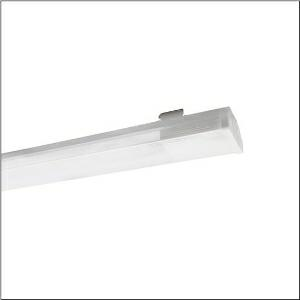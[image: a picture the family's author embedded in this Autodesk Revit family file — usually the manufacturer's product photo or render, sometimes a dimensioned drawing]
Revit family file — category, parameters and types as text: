
# Revit family: modario_r__31_gen_2_53bm811du4gxc2_c2e7
name_source: partatom
category: Lighting Fixtures
units: mm (PartAtom-declared; Revit-internal decimal feet)

## family parameters
Cut with Voids When Loaded = No
Host = Face
Light Source = No
Part Type = Normal
Room Calculation Point = No
Round Connector Dimension = Use Diameter
Shared = No

## types (1)
- --- (1 x LED, 16290 lm, 92.1 W, 4000K)
    Apparent Load = 92 VA
    CIE Flux Codes = 50 78 94 90 100
    Color Rendering = 80
    Color Temperature = 4000K
    Default Elevation = 1800 mm
    Description = Modario® 31 Gen.2, luminaire insert, of sheet steel, coil coated, white, length: 2.392mm, width: 81mm, height: 82mm, 8x system unit, system units: 299mm, LED rated luminous flux: 16.290lm, light colour: 840, control gear: DALI 2, control gear: ECG DALI, with plug, 5-pole, with phase selection, mains connection: 220..240V, AC, 50/60Hz, rated input power: 92W, through-wiring accessed according to module size, primary optical cover: cover, of PMMA, light emission: direct distribution, primary light characteristic: symmetric, protection rating (complete): IP20, protection rating (LED compartment): IP50, insulation class (complete): insulation class I (protective earthing), certification: CE, ENEC, VDE, UKCA, impact resistance: IK03, permissible ambient temperature for indoor applications: -25..+40°C, corresponds to IFS (International Featured Standards) requirements for safety and quality in the food industry, reducing of maximum allowable ambient temperature of 5°C with ceiling mounting, packaging unit: 1 piece
    Height = 92 mm
    Lamp = 1 x LED
    Lamp Light Flux = 16290 lm
    Lamp Power = 92.1 W
    Lamp count = 1
    Length = 2392 mm
    Luminous efficacy = 177 lm/W
    Manufacturer = Siteco
    ModVariant = No
    Model = 53BM811DU4GXC2
    Mounting Place = Ceiling
    Mounting Type = Pendant
    Number of Poles = 1
    OnlyDefault = Yes
    Power Factor = 1
    Product Name = Modario® 31 Gen.2
    Product group = luminaire insert | ceiling pendant
    ProductGroupID = 902
    Protection Class = Protection class I
    Protection Degree = IP 20
    RLX_Detail_Level = 1
    RLX_Emergency_Light_Flux = 0 lm
    RLX_Emergency_Type = 0
    RLX_Emergency_Type_DB = No
    RlxData = <blob elided: 38089 chars, md5=6988f970>
    Socket = socket
    Standby Power = 0 W
    System Light Flux = 16290 lm
    System Power = 92 W
    Type Comments = factory setting: luminous flux: 100 % | dim-lin: 254 | 418 mA
    Type Image = l_1341883.jpg
    URL = http://relux.com
    VarID = @adj_064755
    Voltage = 0 V
    Weight = 0.00 kg
    Width = 81 mm

## geometry (parser evidence)
native form markers: Blend x4, Sweep x13
no freeform markers — native parametric forms only
